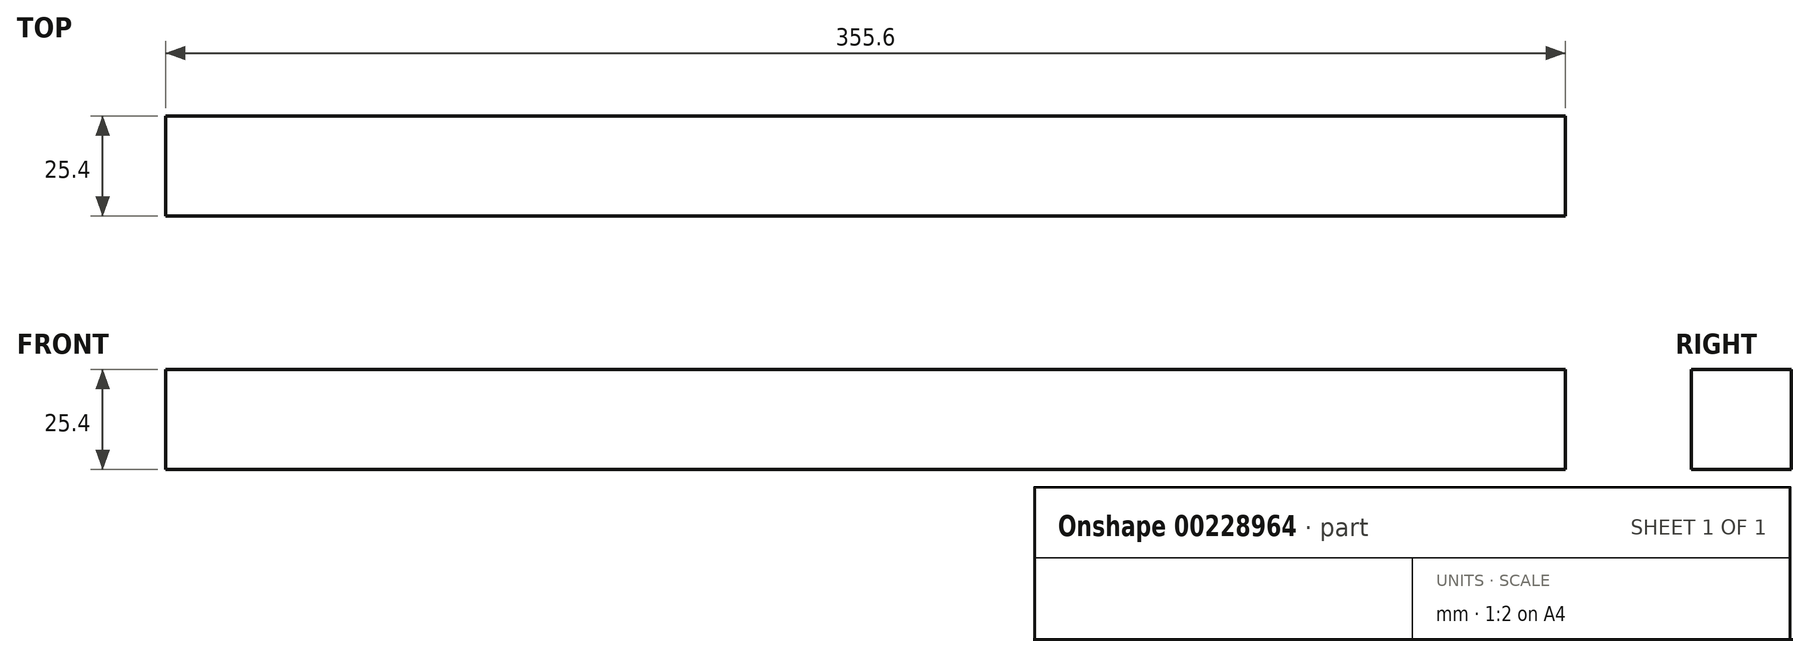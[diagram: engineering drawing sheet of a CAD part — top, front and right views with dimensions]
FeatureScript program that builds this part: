
annotation { "Feature Type Name" : "Feature", "Feature Type Description" : "" }
export const myFeature = defineFeature(function(context is Context, id is Id, definition is map)
    precondition{}
    {
        {
            var Q0;
            Q0=qCreatedBy(makeId("Top.planeOp"),FACE);
            var sketch = newSketch(context, id + "F0", { "sketchPlane" : qUnion([Q0])});
            skLineSegment(sketch, "E0.bottom", {"start": v(0, 0) * mm, "end": v(355.6, 0) * mm});
            skLineSegment(sketch, "E0.top", {"start": v(0, 25.4) * mm, "end": v(355.6, 25.4) * mm});
            skLineSegment(sketch, "E0.left", {"start": v(0, 0) * mm, "end": v(0, 25.4) * mm});
            skLineSegment(sketch, "E0.right", {"start": v(355.6, 0) * mm, "end": v(355.6, 25.4) * mm});
            skSolve(sketch);
        }
        {
            var Q0;
            Q0 = qSketchRegion(id + "F0", true);
            extrude(context, id + "F1", {"entities" : qUnion([Q0]), "depth" : 25.4 * mm});
        }
    });
